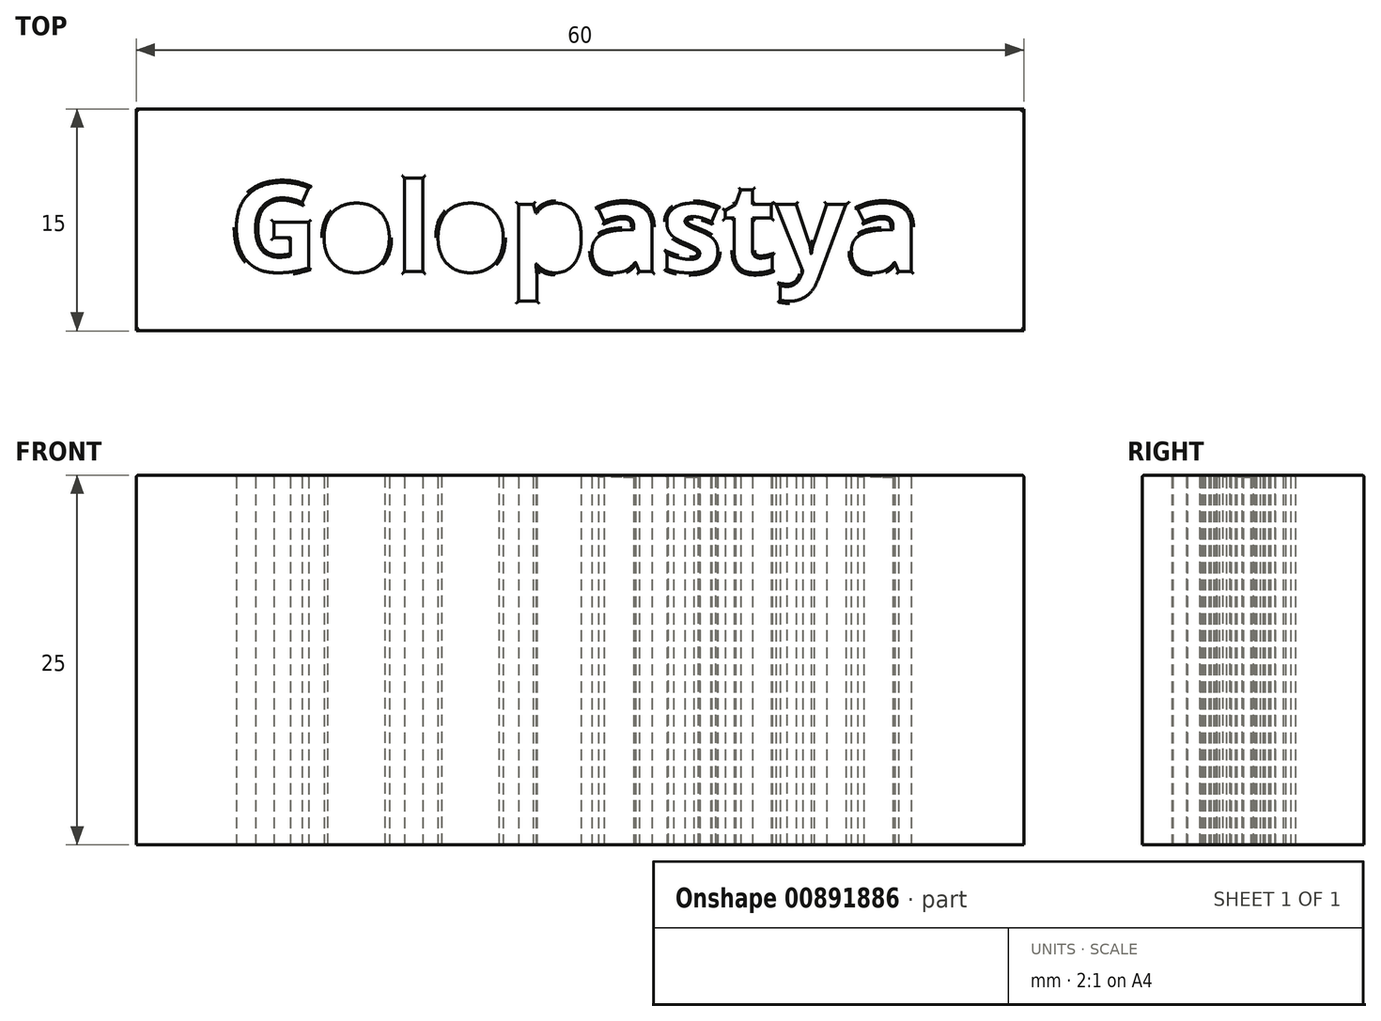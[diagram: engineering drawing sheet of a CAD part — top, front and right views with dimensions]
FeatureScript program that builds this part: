
annotation { "Feature Type Name" : "Feature", "Feature Type Description" : "" }
export const myFeature = defineFeature(function(context is Context, id is Id, definition is map)
    precondition{}
    {
        {
            var Q0;
            Q0=qCreatedBy(makeId("Top.planeOp"),FACE);
            var sketch = newSketch(context, id + "F0", { "sketchPlane" : qUnion([Q0])});
            skLineSegment(sketch, "E0.bottom", {"start": v(-20, 8.84) * mm, "end": v(40, 8.84) * mm});
            skLineSegment(sketch, "E0.top", {"start": v(-20, -6.16) * mm, "end": v(40, -6.16) * mm});
            skLineSegment(sketch, "E0.left", {"start": v(-20, 8.84) * mm, "end": v(-20, -6.16) * mm});
            skLineSegment(sketch, "E0.right", {"start": v(40, 8.84) * mm, "end": v(40, -6.16) * mm});
            skText(sketch, "E1", { "text": "Golopastya", "fontName": "OpenSans-Bold.ttf"});
            const initialGuessF0  = {"E1": [-0.01372, -0.00215, 1, 0, 0.006]};
            skSetInitialGuess(sketch, initialGuessF0);
            skSolve(sketch);
        }
        {
            var Q0;
            Q0=makeQuery(id+"F0.imprint","IMPRINT",FACE,{"disambiguationData":[TD([[makeQuery(id+"F0.imprint","IMPRINT",EDGE,{"derivedFrom":sQuery(id+"F0.wireOp",EDGE,"E0.bottom")}),-1.0]])]});
            extrude(context, id + "F1", {"entities" : qUnion([Q0]), "depth" : 25 * mm, "offsetDistance" : 25 * mm});
        }
        {
            var Q0;
            Q0=makeQuery(id+"F1.opExtrude","CAP_FACE",FACE,{"disambiguationData":[OSD([sQuery(id+"F0.wireOp",EDGE,"E0.bottom"),sQuery(id+"F0.wireOp",EDGE,"E0.top"),sQuery(id+"F0.wireOp",EDGE,"E0.left"),sQuery(id+"F0.wireOp",EDGE,"E0.right"),sQuery(id+"F0.wireOp",EDGE,"E1.sketch_text.stroke-0"),sQuery(id+"F0.wireOp",EDGE,"E1.sketch_text.stroke-1"),sQuery(id+"F0.wireOp",EDGE,"E1.sketch_text.stroke-2"),sQuery(id+"F0.wireOp",EDGE,"E1.sketch_text.stroke-3"),sQuery(id+"F0.wireOp",EDGE,"E1.sketch_text.stroke-4"),sQuery(id+"F0.wireOp",EDGE,"E1.sketch_text.stroke-5"),sQuery(id+"F0.wireOp",EDGE,"E1.sketch_text.stroke-6"),sQuery(id+"F0.wireOp",EDGE,"E1.sketch_text.stroke-7"),sQuery(id+"F0.wireOp",EDGE,"E1.sketch_text.stroke-8"),sQuery(id+"F0.wireOp",EDGE,"E1.sketch_text.stroke-9"),sQuery(id+"F0.wireOp",EDGE,"E1.sketch_text.stroke-10"),sQuery(id+"F0.wireOp",EDGE,"E1.sketch_text.stroke-11"),sQuery(id+"F0.wireOp",EDGE,"E1.sketch_text.stroke-12"),sQuery(id+"F0.wireOp",EDGE,"E1.sketch_text.stroke-13"),sQuery(id+"F0.wireOp",EDGE,"E1.sketch_text.stroke-14"),sQuery(id+"F0.wireOp",EDGE,"E1.sketch_text.stroke-15"),sQuery(id+"F0.wireOp",EDGE,"E1.sketch_text.stroke-16"),sQuery(id+"F0.wireOp",EDGE,"E1.sketch_text.stroke-17"),sQuery(id+"F0.wireOp",EDGE,"E1.sketch_text.stroke-18"),sQuery(id+"F0.wireOp",EDGE,"E1.sketch_text.stroke-19"),sQuery(id+"F0.wireOp",EDGE,"E1.sketch_text.stroke-20"),sQuery(id+"F0.wireOp",EDGE,"E1.sketch_text.stroke-21"),sQuery(id+"F0.wireOp",EDGE,"E1.sketch_text.stroke-22"),sQuery(id+"F0.wireOp",EDGE,"E1.sketch_text.stroke-23"),sQuery(id+"F0.wireOp",EDGE,"E1.sketch_text.stroke-24"),sQuery(id+"F0.wireOp",EDGE,"E1.sketch_text.stroke-25"),sQuery(id+"F0.wireOp",EDGE,"E1.sketch_text.stroke-26"),sQuery(id+"F0.wireOp",EDGE,"E1.sketch_text.stroke-27"),sQuery(id+"F0.wireOp",EDGE,"E1.sketch_text.stroke-28"),sQuery(id+"F0.wireOp",EDGE,"E1.sketch_text.stroke-37"),sQuery(id+"F0.wireOp",EDGE,"E1.sketch_text.stroke-38"),sQuery(id+"F0.wireOp",EDGE,"E1.sketch_text.stroke-39"),sQuery(id+"F0.wireOp",EDGE,"E1.sketch_text.stroke-40"),sQuery(id+"F0.wireOp",EDGE,"E1.sketch_text.stroke-41"),sQuery(id+"F0.wireOp",EDGE,"E1.sketch_text.stroke-42"),sQuery(id+"F0.wireOp",EDGE,"E1.sketch_text.stroke-43"),sQuery(id+"F0.wireOp",EDGE,"E1.sketch_text.stroke-44"),sQuery(id+"F0.wireOp",EDGE,"E1.sketch_text.stroke-45"),sQuery(id+"F0.wireOp",EDGE,"E1.sketch_text.stroke-46"),sQuery(id+"F0.wireOp",EDGE,"E1.sketch_text.stroke-47"),sQuery(id+"F0.wireOp",EDGE,"E1.sketch_text.stroke-48"),sQuery(id+"F0.wireOp",EDGE,"E1.sketch_text.stroke-49"),sQuery(id+"F0.wireOp",EDGE,"E1.sketch_text.stroke-58"),sQuery(id+"F0.wireOp",EDGE,"E1.sketch_text.stroke-59"),sQuery(id+"F0.wireOp",EDGE,"E1.sketch_text.stroke-60"),sQuery(id+"F0.wireOp",EDGE,"E1.sketch_text.stroke-61"),sQuery(id+"F0.wireOp",EDGE,"E1.sketch_text.stroke-62"),sQuery(id+"F0.wireOp",EDGE,"E1.sketch_text.stroke-63"),sQuery(id+"F0.wireOp",EDGE,"E1.sketch_text.stroke-64"),sQuery(id+"F0.wireOp",EDGE,"E1.sketch_text.stroke-65"),sQuery(id+"F0.wireOp",EDGE,"E1.sketch_text.stroke-66"),sQuery(id+"F0.wireOp",EDGE,"E1.sketch_text.stroke-67"),sQuery(id+"F0.wireOp",EDGE,"E1.sketch_text.stroke-68"),sQuery(id+"F0.wireOp",EDGE,"E1.sketch_text.stroke-69"),sQuery(id+"F0.wireOp",EDGE,"E1.sketch_text.stroke-70"),sQuery(id+"F0.wireOp",EDGE,"E1.sketch_text.stroke-71"),sQuery(id+"F0.wireOp",EDGE,"E1.sketch_text.stroke-72"),sQuery(id+"F0.wireOp",EDGE,"E1.sketch_text.stroke-73"),sQuery(id+"F0.wireOp",EDGE,"E1.sketch_text.stroke-83"),sQuery(id+"F0.wireOp",EDGE,"E1.sketch_text.stroke-84"),sQuery(id+"F0.wireOp",EDGE,"E1.sketch_text.stroke-85"),sQuery(id+"F0.wireOp",EDGE,"E1.sketch_text.stroke-86"),sQuery(id+"F0.wireOp",EDGE,"E1.sketch_text.stroke-87"),sQuery(id+"F0.wireOp",EDGE,"E1.sketch_text.stroke-88"),sQuery(id+"F0.wireOp",EDGE,"E1.sketch_text.stroke-89"),sQuery(id+"F0.wireOp",EDGE,"E1.sketch_text.stroke-90"),sQuery(id+"F0.wireOp",EDGE,"E1.sketch_text.stroke-91"),sQuery(id+"F0.wireOp",EDGE,"E1.sketch_text.stroke-92"),sQuery(id+"F0.wireOp",EDGE,"E1.sketch_text.stroke-93"),sQuery(id+"F0.wireOp",EDGE,"E1.sketch_text.stroke-94"),sQuery(id+"F0.wireOp",EDGE,"E1.sketch_text.stroke-95"),sQuery(id+"F0.wireOp",EDGE,"E1.sketch_text.stroke-96"),sQuery(id+"F0.wireOp",EDGE,"E1.sketch_text.stroke-97"),sQuery(id+"F0.wireOp",EDGE,"E1.sketch_text.stroke-98"),sQuery(id+"F0.wireOp",EDGE,"E1.sketch_text.stroke-99"),sQuery(id+"F0.wireOp",EDGE,"E1.sketch_text.stroke-100"),sQuery(id+"F0.wireOp",EDGE,"E1.sketch_text.stroke-101"),sQuery(id+"F0.wireOp",EDGE,"E1.sketch_text.stroke-110"),sQuery(id+"F0.wireOp",EDGE,"E1.sketch_text.stroke-111"),sQuery(id+"F0.wireOp",EDGE,"E1.sketch_text.stroke-112"),sQuery(id+"F0.wireOp",EDGE,"E1.sketch_text.stroke-113"),sQuery(id+"F0.wireOp",EDGE,"E1.sketch_text.stroke-114"),sQuery(id+"F0.wireOp",EDGE,"E1.sketch_text.stroke-115"),sQuery(id+"F0.wireOp",EDGE,"E1.sketch_text.stroke-116"),sQuery(id+"F0.wireOp",EDGE,"E1.sketch_text.stroke-117"),sQuery(id+"F0.wireOp",EDGE,"E1.sketch_text.stroke-118"),sQuery(id+"F0.wireOp",EDGE,"E1.sketch_text.stroke-119"),sQuery(id+"F0.wireOp",EDGE,"E1.sketch_text.stroke-120"),sQuery(id+"F0.wireOp",EDGE,"E1.sketch_text.stroke-121"),sQuery(id+"F0.wireOp",EDGE,"E1.sketch_text.stroke-122"),sQuery(id+"F0.wireOp",EDGE,"E1.sketch_text.stroke-123"),sQuery(id+"F0.wireOp",EDGE,"E1.sketch_text.stroke-124"),sQuery(id+"F0.wireOp",EDGE,"E1.sketch_text.stroke-125"),sQuery(id+"F0.wireOp",EDGE,"E1.sketch_text.stroke-126"),sQuery(id+"F0.wireOp",EDGE,"E1.sketch_text.stroke-127"),sQuery(id+"F0.wireOp",EDGE,"E1.sketch_text.stroke-128"),sQuery(id+"F0.wireOp",EDGE,"E1.sketch_text.stroke-129"),sQuery(id+"F0.wireOp",EDGE,"E1.sketch_text.stroke-130"),sQuery(id+"F0.wireOp",EDGE,"E1.sketch_text.stroke-131"),sQuery(id+"F0.wireOp",EDGE,"E1.sketch_text.stroke-132"),sQuery(id+"F0.wireOp",EDGE,"E1.sketch_text.stroke-133"),sQuery(id+"F0.wireOp",EDGE,"E1.sketch_text.stroke-134"),sQuery(id+"F0.wireOp",EDGE,"E1.sketch_text.stroke-135"),sQuery(id+"F0.wireOp",EDGE,"E1.sketch_text.stroke-136"),sQuery(id+"F0.wireOp",EDGE,"E1.sketch_text.stroke-137"),sQuery(id+"F0.wireOp",EDGE,"E1.sketch_text.stroke-138"),sQuery(id+"F0.wireOp",EDGE,"E1.sketch_text.stroke-139"),sQuery(id+"F0.wireOp",EDGE,"E1.sketch_text.stroke-140"),sQuery(id+"F0.wireOp",EDGE,"E1.sketch_text.stroke-141"),sQuery(id+"F0.wireOp",EDGE,"E1.sketch_text.stroke-142"),sQuery(id+"F0.wireOp",EDGE,"E1.sketch_text.stroke-143"),sQuery(id+"F0.wireOp",EDGE,"E1.sketch_text.stroke-144"),sQuery(id+"F0.wireOp",EDGE,"E1.sketch_text.stroke-145"),sQuery(id+"F0.wireOp",EDGE,"E1.sketch_text.stroke-146"),sQuery(id+"F0.wireOp",EDGE,"E1.sketch_text.stroke-147"),sQuery(id+"F0.wireOp",EDGE,"E1.sketch_text.stroke-148"),sQuery(id+"F0.wireOp",EDGE,"E1.sketch_text.stroke-149"),sQuery(id+"F0.wireOp",EDGE,"E1.sketch_text.stroke-150"),sQuery(id+"F0.wireOp",EDGE,"E1.sketch_text.stroke-151"),sQuery(id+"F0.wireOp",EDGE,"E1.sketch_text.stroke-152"),sQuery(id+"F0.wireOp",EDGE,"E1.sketch_text.stroke-153"),sQuery(id+"F0.wireOp",EDGE,"E1.sketch_text.stroke-154"),sQuery(id+"F0.wireOp",EDGE,"E1.sketch_text.stroke-155"),sQuery(id+"F0.wireOp",EDGE,"E1.sketch_text.stroke-156"),sQuery(id+"F0.wireOp",EDGE,"E1.sketch_text.stroke-157"),sQuery(id+"F0.wireOp",EDGE,"E1.sketch_text.stroke-158"),sQuery(id+"F0.wireOp",EDGE,"E1.sketch_text.stroke-159"),sQuery(id+"F0.wireOp",EDGE,"E1.sketch_text.stroke-160"),sQuery(id+"F0.wireOp",EDGE,"E1.sketch_text.stroke-161"),sQuery(id+"F0.wireOp",EDGE,"E1.sketch_text.stroke-162"),sQuery(id+"F0.wireOp",EDGE,"E1.sketch_text.stroke-163"),sQuery(id+"F0.wireOp",EDGE,"E1.sketch_text.stroke-164"),sQuery(id+"F0.wireOp",EDGE,"E1.sketch_text.stroke-165"),sQuery(id+"F0.wireOp",EDGE,"E1.sketch_text.stroke-166"),sQuery(id+"F0.wireOp",EDGE,"E1.sketch_text.stroke-167"),sQuery(id+"F0.wireOp",EDGE,"E1.sketch_text.stroke-168"),sQuery(id+"F0.wireOp",EDGE,"E1.sketch_text.stroke-169"),sQuery(id+"F0.wireOp",EDGE,"E1.sketch_text.stroke-170"),sQuery(id+"F0.wireOp",EDGE,"E1.sketch_text.stroke-171"),sQuery(id+"F0.wireOp",EDGE,"E1.sketch_text.stroke-172"),sQuery(id+"F0.wireOp",EDGE,"E1.sketch_text.stroke-173"),sQuery(id+"F0.wireOp",EDGE,"E1.sketch_text.stroke-174"),sQuery(id+"F0.wireOp",EDGE,"E1.sketch_text.stroke-175"),sQuery(id+"F0.wireOp",EDGE,"E1.sketch_text.stroke-176"),sQuery(id+"F0.wireOp",EDGE,"E1.sketch_text.stroke-177"),sQuery(id+"F0.wireOp",EDGE,"E1.sketch_text.stroke-178"),sQuery(id+"F0.wireOp",EDGE,"E1.sketch_text.stroke-179"),sQuery(id+"F0.wireOp",EDGE,"E1.sketch_text.stroke-180"),sQuery(id+"F0.wireOp",EDGE,"E1.sketch_text.stroke-181"),sQuery(id+"F0.wireOp",EDGE,"E1.sketch_text.stroke-182"),sQuery(id+"F0.wireOp",EDGE,"E1.sketch_text.stroke-183"),sQuery(id+"F0.wireOp",EDGE,"E1.sketch_text.stroke-184"),sQuery(id+"F0.wireOp",EDGE,"E1.sketch_text.stroke-185"),sQuery(id+"F0.wireOp",EDGE,"E1.sketch_text.stroke-186"),sQuery(id+"F0.wireOp",EDGE,"E1.sketch_text.stroke-187"),sQuery(id+"F0.wireOp",EDGE,"E1.sketch_text.stroke-188")])],"isStart":false});
            fillet(context, id + "F2", {"entities" : qUnion([Q0]), "radius" : .15 * mm, "allowEdgeOverflow" : false});
        }
    });
